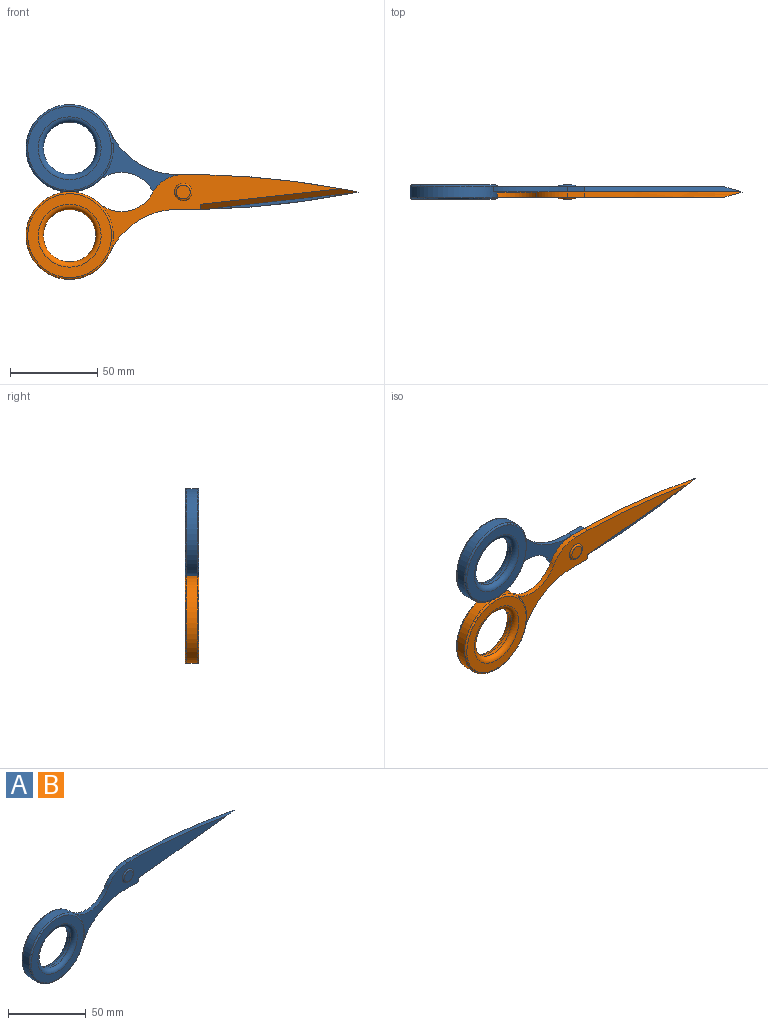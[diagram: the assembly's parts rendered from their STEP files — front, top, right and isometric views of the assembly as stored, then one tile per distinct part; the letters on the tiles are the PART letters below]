
ASSEMBLY  parts=2 mates=1
PART A: 20 faces, bbox 192.1x8x62.1 mm
  f0: plane 138.65x45.22mm, normal (0,-1,0), area 1468.6mm2, adj f2,f3,f4,f5,f6,f8,f13,f14
  f1: plane 148.49x45.22mm, normal (0,1,0), area 1802.5mm2, adj f2,f3,f4,f5,f6,f7,f8,f13
  f2: plane 10x3mm, normal (0,0,1), area 30mm2, adj f0,f1,f4,f5
  f3: plane 10x3mm, normal (0,0,-1), area 30mm2, adj f0,f1,f8,f14
  f4: cylinder r=500mm len=90mm, axis (0,1,0), area 257.2mm2, adj f0,f1,f2,f13
  f5: cylinder r=20mm len=17.32mm, axis (0,1,0), area 62.8mm2, adj f0,f1,f2,f6
  f6: cylinder r=20mm len=31.17mm, axis (0,1,0), area 110.2mm2, adj f0,f1,f5,f7
  f7: cylinder r=25mm len=50mm, axis (0,1,0), area 847.2mm2, adj f1,f6,f8,f18,f19
  f8: cylinder r=42.84mm len=42.18mm, axis (0,1,0), area 157mm2, adj f0,f1,f3,f7
  f9: plane 48x48mm, normal (0,1,0), area 791.7mm2, adj f15,f18
  f10: cylinder r=15mm len=30mm, axis (0,1,0), area 188.5mm2, adj f15,f16
  f11: plane 48x48mm, normal (0,-1,0), area 791.7mm2, adj f16,f19
  f12: plane 8x8mm, normal (0,-1,0), area 50.3mm2, adj f17
  f13: plane 90x11.91mm, normal (0.08,-0.7,-0.7), area 362.3mm2, adj f0,f1,f4,f14
  f14: plane 3x3mm, normal (1,0,0), area 4.5mm2, adj f0,f3,f13
  f15: torus R=18mm, axis (0,-1,0), area 476.4mm2, adj f9,f10
  f16: torus R=18mm, axis (0,-1,0), area 476.4mm2, adj f10,f11
  f17: torus R=4mm, axis (0,-1,0), area 45.8mm2, adj f0,f12
  f18: torus R=24mm, axis (0,-1,0), area 243.2mm2, adj f7,f9
  f19: torus R=24mm, axis (0,-1,0), area 243.2mm2, adj f0,f7,f11
PART B: same geometry as A
PLACE A rot(axis=(1,0,0),180deg) t=(-1.67,-27.12,-23.57)mm
PLACE B t=(-1.67,-27.12,-23.57)mm fixed
MATE revolute B.f17 <-> A.f17  axis (0,-1,0) through (-1.67,-27.12,-23.57)mm
